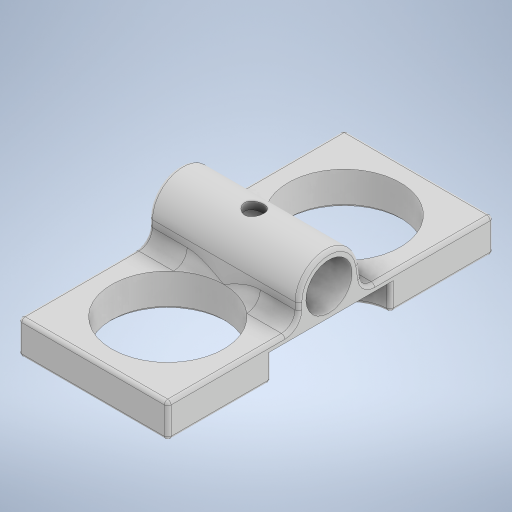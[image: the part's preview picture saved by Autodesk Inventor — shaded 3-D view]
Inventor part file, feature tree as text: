
AUTODESK INVENTOR PART (.ipt)
format: ipt  version: 2024.2 (Build 282272000, 272)  size: 433,152 bytes
history: native  units: mm
features: extrude x5, sketch x4, fillet x3, chamfer x1, plane x1
ambient origin geometry x8: Origin, YZ Plane, XZ Plane, XY Plane, X Axis, Y Axis, Z Axis, Center Point
bodies: Solid1 (feature_tree)
feature tree (14):
  extrude  "Extrusion1"  Depth=26.0mm
  sketch  "Sketch2"  dims[d2=13.0mm d3=11.0mm]
  extrude  "Extrusion2"  Depth=11.0mm
  extrude  "Extrusion3"  Depth=11.0mm
  extrude  "Extrusion4"  Depth=10.0mm TaperAngle=0.0deg
  fillet  "Fillet1"  Radius=6.8mm
  fillet  "Fillet2"  Radius=9.0mm
  fillet  "Fillet3"  Radius=8.0mm
  chamfer  "Chamfer1"  Distance=3.0mm
  plane  "Work Plane1"
  extrude  "Extrusion5"  TaperAngle=0.0deg  [1 undecoded]
  sketch  "Sketch1"  dims[d0=16.5mm d1=26.0mm]
  sketch  "Sketch3"  dims[d4=11.0mm d5=11.0mm]
  sketch  "Sketch4"  dims[d6=11.0mm d7=5.0mm d8=0.0mm d9=6.8mm d10=9.0mm d11=8.0mm d12=3.0mm d13=0.0mm d14=0.0mm d15=0.0mm d18=12.5mm d19=5.0mm d20=4.0mm d21=0.0mm d22=2.0mm d23=0.5mm d24=0.5mm d25=0.5mm d26=2.0mm d27=45.0deg d28=10.0mm d29=2.8mm d30=2.0mm d31=0.0mm]
note: 1 required parameter value undecoded (feature->parameter linkage not recoverable at this tier; creation-order binding heuristic only, values carry confidence <= 0.55)
